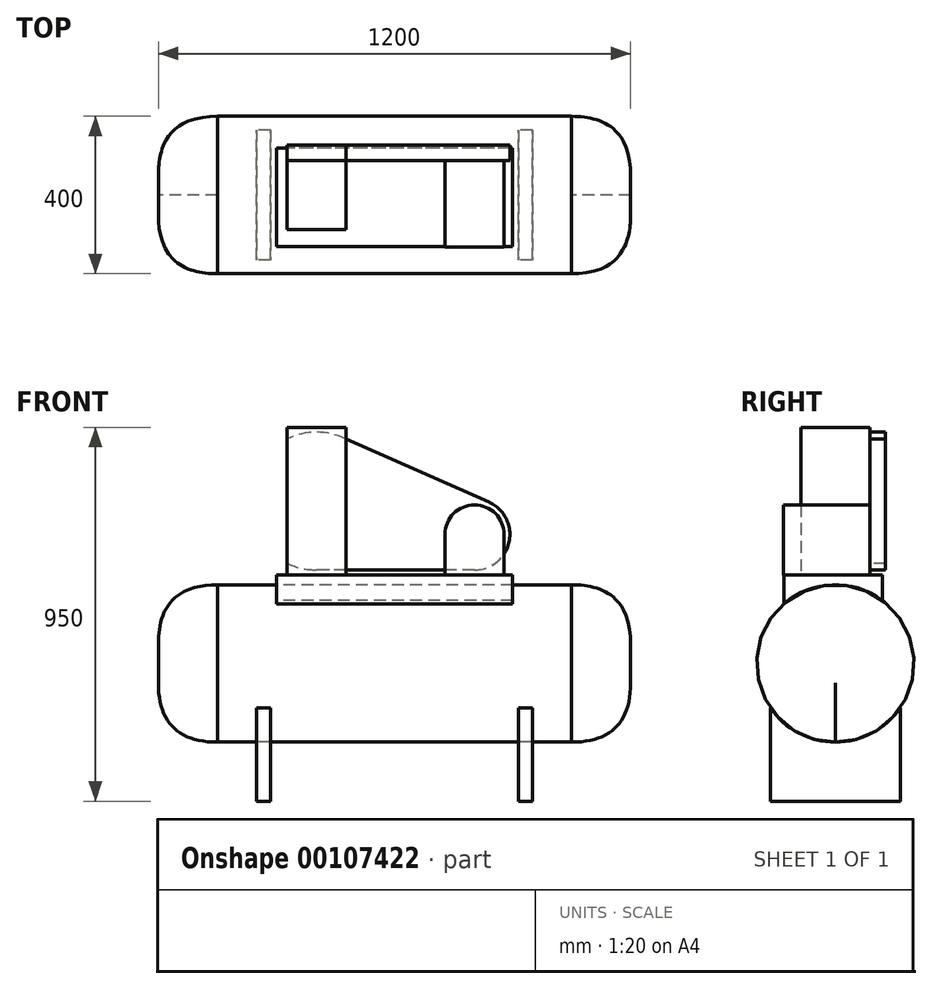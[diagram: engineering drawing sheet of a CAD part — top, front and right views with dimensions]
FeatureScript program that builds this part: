
annotation { "Feature Type Name" : "Feature", "Feature Type Description" : "" }
export const myFeature = defineFeature(function(context is Context, id is Id, definition is map)
    precondition{}
    {
        {
            var Q0;
            Q0=qCreatedBy(makeId("Right.planeOp"),FACE);
            var sketch = newSketch(context, id + "F0", { "sketchPlane" : qUnion([Q0])});
            skCircle(sketch, "E0", {"center": v(0, 0) * mm, "radius": 200 * mm});
            skLineSegment(sketch, "E1", {"start": v(0, 0) * mm, "end": v(0, 200) * mm});
            skLineSegment(sketch, "E2", {"start": v(0, 0) * mm, "end": v(0, -200) * mm});
            skSolve(sketch);
        }
        {
            var Q0;
            Q0=makeQuery(id+"F0.imprint","IMPRINT",FACE,{"disambiguationData":[TD([[makeQuery(id+"F0.imprint","IMPRINT",EDGE,{"derivedFrom":sQuery(id+"F0.wireOp",EDGE,"E0")}),1.0]])]});
            extrude(context, id + "F1", {"entities" : qUnion([Q0]), "endBound" : BoundingType.SYMMETRIC, "depth" : 1200 * mm});
        }
        {
            var Q0;
            Q0=makeQuery(id+"F1.opExtrude","CAP_EDGE",EDGE,{"disambiguationData":[OSD([sQuery(id+"F0.wireOp",EDGE,"E0")])],"isStart":false});
            var Q1;
            Q1=makeQuery(id+"F1.opExtrude","CAP_EDGE",EDGE,{"disambiguationData":[OSD([sQuery(id+"F0.wireOp",EDGE,"E0")])],"isStart":true});
            fillet(context, id + "F2", {"entities" : qUnion([Q0, Q1]), "radius" : 150 * mm, "tangentPropagation" : true, "rho" : .5, "crossSection" : FilletCrossSection.CONIC, "allowEdgeOverflow" : false});
        }
        {
            var Q0;
            Q0=sQuery(id+"F0.wireOp",VERTEX,"E1.end");
            var Q1;
            Q1=sQuery(id+"F0.wireOp",EDGE,"E1");
            cPlane(context, id + "F3", {"entities" : qUnion([Q0, Q1]), "cplaneType" : CPlaneType.LINE_POINT, "offset" : 25 * mm, "width" : 150 * mm, "height" : 150 * mm});
        }
        {
            var Q0;
            Q0=qCreatedBy(id+"F3.planeOp",FACE);
            cPlane(context, id + "F4", {"entities" : qUnion([Q0]), "cplaneType" : CPlaneType.OFFSET, "offset" : 25 * mm, "width" : 150 * mm, "height" : 150 * mm});
        }
        {
            var Q0;
            Q0=qCreatedBy(id+"F4.planeOp",FACE);
            var sketch = newSketch(context, id + "F5", { "sketchPlane" : qUnion([Q0])});
            skLineSegment(sketch, "E3.bottom", {"start": v(300, -130.85) * mm, "end": v(-300, -130.85) * mm});
            skLineSegment(sketch, "E3.top", {"start": v(300, 119.15) * mm, "end": v(-300, 119.15) * mm});
            skLineSegment(sketch, "E3.left", {"start": v(300, -130.85) * mm, "end": v(300, 119.15) * mm});
            skLineSegment(sketch, "E3.right", {"start": v(-300, -130.85) * mm, "end": v(-300, 119.15) * mm});
            skPoint(sketch, "E3.middle", {"position": v(0, -5.85) * mm});
            skSolve(sketch);
        }
        {
            var Q0;
            Q0=makeQuery(id+"F5.imprint","IMPRINT",FACE,{"disambiguationData":[TD([[makeQuery(id+"F5.imprint","IMPRINT",EDGE,{"derivedFrom":sQuery(id+"F5.wireOp",EDGE,"E3.bottom")}),-1.0]])]});
            extrude(context, id + "F6", {"entities" : qUnion([Q0]), "endBound" : BoundingType.UP_TO_NEXT, "oppositeDirection" : true, "depth" : 25 * mm});
        }
        {
            var Q0;
            Q0=makeQuery(id+"F6.opExtrude","CAP_FACE",FACE,{"disambiguationData":[OSD([sQuery(id+"F5.wireOp",EDGE,"E3.bottom"),sQuery(id+"F5.wireOp",EDGE,"E3.top"),sQuery(id+"F5.wireOp",EDGE,"E3.left"),sQuery(id+"F5.wireOp",EDGE,"E3.right")])],"isStart":true});
            var sketch = newSketch(context, id + "F7", { "sketchPlane" : qUnion([Q0])});
            skLineSegment(sketch, "E4.bottom", {"start": v(-273, 87.5) * mm, "end": v(-123, 87.5) * mm});
            skLineSegment(sketch, "E4.top", {"start": v(-273, -87.5) * mm, "end": v(-123, -87.5) * mm});
            skLineSegment(sketch, "E4.left", {"start": v(-273, 87.5) * mm, "end": v(-273, -87.5) * mm});
            skLineSegment(sketch, "E4.right", {"start": v(-123, 87.5) * mm, "end": v(-123, -87.5) * mm});
            skPoint(sketch, "E4.middle", {"position": v(-198, 0) * mm});
            skSolve(sketch);
        }
        {
            var Q0;
            Q0=makeQuery(id+"F7.imprint","IMPRINT",FACE,{"disambiguationData":[TD([[makeQuery(id+"F7.imprint","IMPRINT",EDGE,{"derivedFrom":sQuery(id+"F7.wireOp",EDGE,"E4.bottom")}),-1.0]])]});
            extrude(context, id + "F8", {"entities" : qUnion([Q0]), "depth" : 375 * mm});
        }
        {
            var Q0;
            Q0=makeQuery(id+"F8.opExtrude","SWEPT_FACE",FACE,{"disambiguationData":[OSD([sQuery(id+"F7.wireOp",EDGE,"E4.bottom")])]});
            var sketch = newSketch(context, id + "F9", { "sketchPlane" : qUnion([Q0])});
            skCircle(sketch, "E5", {"center": v(198, 412.5) * mm, "radius": 175 * mm});
            skPoint(sketch, "E5.centerSnap0", {"position": v(198, 600) * mm});
            skPoint(sketch, "E5.centerSnap1", {"position": v(273, 412.5) * mm});
            skCircle(sketch, "E6", {"center": v(-203.22, 327.5) * mm, "radius": 90 * mm});
            skLineSegment(sketch, "E7", {"start": v(-239.72, 409.77) * mm, "end": v(127.04, 572.47) * mm});
            skLineSegment(sketch, "E8", {"start": v(-203.22, 237.5) * mm, "end": v(198, 237.5) * mm});
            skCircle(sketch, "E9", {"center": v(-203.22, 327.5) * mm, "radius": 75 * mm});
            skLineSegment(sketch, "E10.0.0", {"start": v(300, 225) * mm, "end": v(-300, 225) * mm});
            skLineSegment(sketch, "E10.0.2", {"start": v(-300, 225) * mm, "end": v(300, 225) * mm});
            skLineSegment(sketch, "E11", {"start": v(-128.22, 327.5) * mm, "end": v(-128.22, 225) * mm});
            skLineSegment(sketch, "E12", {"start": v(-278.22, 327.5) * mm, "end": v(-278.22, 225) * mm});
            skSolve(sketch);
        }
        {
            var Q0;
            {var subQ0=sQuery(id+"F9.wireOp",EDGE,"E6");var subQ1=makeQuery(id+"F9.imprint","INTERSECT",VERTEX,{"derivedFrom":[subQ0,sQuery(id+"F9.wireOp",EDGE,"E7")]});Q0=makeQuery(id+"F9.imprint","IMPRINT",FACE,{"disambiguationData":[TD([[makeQuery(id+"F9.imprint","IMPRINT",EDGE,{"disambiguationData":[TD([[subQ1,-1.0]])],"derivedFrom":subQ0}),1.0]])]});}
            var Q1;
            {var subQ1=sQuery(id+"F9.wireOp",EDGE,"E6");var subQ7=sQuery(id+"F9.wireOp",EDGE,"E7");var subQ8=makeQuery(id+"F9.imprint","INTERSECT",VERTEX,{"derivedFrom":[subQ1,subQ7]});Q1=makeQuery(id+"F9.imprint","IMPRINT",FACE,{"disambiguationData":[TD([[makeQuery(id+"F9.imprint","IMPRINT",EDGE,{"disambiguationData":[TD([[subQ8,1.0]])],"derivedFrom":subQ1}),-1.0]])]});}
            var Q2;
            {var subQ0=sQuery(id+"F9.wireOp",EDGE,"E5");var subQ1=makeQuery(id+"F8.opExtrude","SWEPT_EDGE",EDGE,{"disambiguationData":[OSD([sQuery(id+"F7.wireOp",EDGE,"E4.bottom"),sQuery(id+"F7.wireOp",EDGE,"E4.right")])]});var subQ2=makeQuery(id+"F9.imprint","INTERSECT",VERTEX,{"disambiguationData":[OD(0.0)],"derivedFrom":[subQ1,subQ0]});Q2=makeQuery(id+"F9.imprint","IMPRINT",FACE,{"disambiguationData":[TD([[makeQuery(id+"F9.imprint","IMPRINT",EDGE,{"disambiguationData":[TD([[subQ2,-1.0]])],"derivedFrom":subQ0}),1.0]])]});}
            var Q3;
            {var subQ0=sQuery(id+"F9.wireOp",EDGE,"E5");var subQ8=makeQuery(id+"F9.imprint","INTERSECT",VERTEX,{"derivedFrom":[subQ0,sQuery(id+"F9.wireOp",EDGE,"E7")]});Q3=makeQuery(id+"F9.imprint","IMPRINT",FACE,{"disambiguationData":[TD([[makeQuery(id+"F9.imprint","IMPRINT",EDGE,{"disambiguationData":[TD([[subQ8,1.0]])],"derivedFrom":subQ0}),1.0]])]});}
            var Q4;
            {var subQ0=sQuery(id+"F9.wireOp",EDGE,"E8");var subQ1=sQuery(id+"F9.wireOp",EDGE,"E5");var subQ2=makeQuery(id+"F9.imprint","INTERSECT",VERTEX,{"derivedFrom":[subQ1,subQ0]});Q4=makeQuery(id+"F9.imprint","IMPRINT",FACE,{"disambiguationData":[TD([[makeQuery(id+"F9.imprint","IMPRINT",EDGE,{"disambiguationData":[TD([[subQ2,1.0]])],"derivedFrom":subQ1}),-1.0]])]});}
            var Q5;
            {var subQ0=sQuery(id+"F9.wireOp",EDGE,"E5");var subQ1=makeQuery(id+"F8.opExtrude","SWEPT_EDGE",EDGE,{"disambiguationData":[OSD([sQuery(id+"F7.wireOp",EDGE,"E4.bottom"),sQuery(id+"F7.wireOp",EDGE,"E4.left")])]});var subQ2=makeQuery(id+"F9.imprint","INTERSECT",VERTEX,{"disambiguationData":[OD(0.0)],"derivedFrom":[subQ1,subQ0]});Q5=makeQuery(id+"F9.imprint","IMPRINT",FACE,{"disambiguationData":[TD([[makeQuery(id+"F9.imprint","IMPRINT",EDGE,{"disambiguationData":[TD([[subQ2,1.0]])],"derivedFrom":subQ0}),1.0]])]});}
            var Q6;
            Q6=makeQuery(id+"F9.imprint","IMPRINT",FACE,{"disambiguationData":[TD([[makeQuery(id+"F9.imprint","IMPRINT",EDGE,{"derivedFrom":sQuery(id+"F9.wireOp",EDGE,"E9")}),1.0]])]});
            var Q7;
            {var subQ5=sQuery(id+"F9.wireOp",EDGE,"E6");var subQ7=makeQuery(id+"F9.imprint","INTERSECT",VERTEX,{"derivedFrom":[subQ5,sQuery(id+"F9.wireOp",EDGE,"E8")]});Q7=makeQuery(id+"F9.imprint","IMPRINT",FACE,{"disambiguationData":[TD([[makeQuery(id+"F9.imprint","IMPRINT",EDGE,{"disambiguationData":[TD([[subQ7,1.0]])],"derivedFrom":subQ5}),1.0]])]});}
            var Q8;
            {var subQ0=sQuery(id+"F9.wireOp",EDGE,"E8");var subQ1=sQuery(id+"F9.wireOp",EDGE,"E6");var subQ2=makeQuery(id+"F9.imprint","INTERSECT",VERTEX,{"derivedFrom":[subQ1,subQ0]});Q8=makeQuery(id+"F9.imprint","IMPRINT",FACE,{"disambiguationData":[TD([[makeQuery(id+"F9.imprint","IMPRINT",EDGE,{"disambiguationData":[TD([[subQ2,-1.0]])],"derivedFrom":subQ1}),-1.0]])]});}
            extrude(context, id + "F10", {"entities" : qUnion([Q0, Q1, Q2, Q3, Q4, Q5, Q6, Q7, Q8]), "depth" : 40 * mm});
        }
        {
            var Q0;
            Q0=makeQuery(id+"F9.imprint","IMPRINT",FACE,{"disambiguationData":[TD([[makeQuery(id+"F9.imprint","IMPRINT",EDGE,{"derivedFrom":sQuery(id+"F9.wireOp",EDGE,"E9")}),1.0]])]});
            var Q1;
            {var subQ0=sQuery(id+"F9.wireOp",EDGE,"E8");var subQ1=sQuery(id+"F9.wireOp",EDGE,"E6");var subQ2=makeQuery(id+"F9.imprint","INTERSECT",VERTEX,{"derivedFrom":[subQ1,subQ0]});Q1=makeQuery(id+"F9.imprint","IMPRINT",FACE,{"disambiguationData":[TD([[makeQuery(id+"F9.imprint","IMPRINT",EDGE,{"disambiguationData":[TD([[subQ2,-1.0]])],"derivedFrom":subQ1}),-1.0]])]});}
            var Q2;
            {var subQ5=sQuery(id+"F9.wireOp",EDGE,"E6");var subQ7=makeQuery(id+"F9.imprint","INTERSECT",VERTEX,{"derivedFrom":[subQ5,sQuery(id+"F9.wireOp",EDGE,"E8")]});Q2=makeQuery(id+"F9.imprint","IMPRINT",FACE,{"disambiguationData":[TD([[makeQuery(id+"F9.imprint","IMPRINT",EDGE,{"disambiguationData":[TD([[subQ7,1.0]])],"derivedFrom":subQ5}),1.0]])]});}
            var Q3;
            {var subQ5=sQuery(id+"F9.wireOp",EDGE,"E8");var subQ6=sQuery(id+"F9.wireOp",EDGE,"E6");var subQ7=makeQuery(id+"F9.imprint","INTERSECT",VERTEX,{"derivedFrom":[subQ6,subQ5]});Q3=makeQuery(id+"F9.imprint","IMPRINT",FACE,{"disambiguationData":[TD([[makeQuery(id+"F9.imprint","IMPRINT",EDGE,{"disambiguationData":[TD([[subQ7,1.0]])],"derivedFrom":subQ6}),-1.0]])]});}
            extrude(context, id + "F11", {"entities" : qUnion([Q0, Q1, Q2, Q3]), "oppositeDirection" : true, "depth" : 220 * mm});
        }
        {
            var Q0;
            Q0=sQuery(id+"F0.wireOp",VERTEX,"E2.end");
            var Q1;
            Q1=sQuery(id+"F0.wireOp",EDGE,"E2");
            cPlane(context, id + "F12", {"entities" : qUnion([Q0, Q1]), "cplaneType" : CPlaneType.LINE_POINT, "offset" : 25 * mm, "width" : 150 * mm, "height" : 150 * mm});
        }
        {
            var Q0;
            Q0=qCreatedBy(id+"F12.planeOp",FACE);
            cPlane(context, id + "F13", {"entities" : qUnion([Q0]), "cplaneType" : CPlaneType.OFFSET, "offset" : 150 * mm, "width" : 150 * mm, "height" : 150 * mm});
        }
        {
            var Q0;
            Q0=qCreatedBy(id+"F13.planeOp",FACE);
            var sketch = newSketch(context, id + "F14", { "sketchPlane" : qUnion([Q0])});
            skLineSegment(sketch, "E13.bottom", {"start": v(315.41, -165.12) * mm, "end": v(350, -165.12) * mm});
            skLineSegment(sketch, "E13.top", {"start": v(315.41, 165.12) * mm, "end": v(350, 165.12) * mm});
            skLineSegment(sketch, "E13.left", {"start": v(315.41, -165.12) * mm, "end": v(315.41, 165.12) * mm});
            skLineSegment(sketch, "E13.right", {"start": v(350, -165.12) * mm, "end": v(350, 165.12) * mm});
            skPoint(sketch, "E13.middle", {"position": v(332.7, 0) * mm});
            skLineSegment(sketch, "E14.0", {"start": v(0, 200) * mm, "end": v(0, -200) * mm});
            skLineSegment(sketch, "E15.MirrorCS", {"start": v(-315.41, -165.12) * mm, "end": v(-315.41, 165.12) * mm});
            skLineSegment(sketch, "E16.MirrorCS", {"start": v(-315.41, 165.12) * mm, "end": v(-350, 165.12) * mm});
            skLineSegment(sketch, "E17.MirrorCS", {"start": v(-350, -165.12) * mm, "end": v(-350, 165.12) * mm});
            skLineSegment(sketch, "E18.MirrorCS", {"start": v(-315.41, -165.12) * mm, "end": v(-350, -165.12) * mm});
            skSolve(sketch);
        }
        {
            var Q0;
            Q0=makeQuery(id+"F14.imprint","IMPRINT",FACE,{"disambiguationData":[TD([[makeQuery(id+"F14.imprint","IMPRINT",EDGE,{"derivedFrom":sQuery(id+"F14.wireOp",EDGE,"E13.bottom")}),1.0]])]});
            var Q1;
            Q1=makeQuery(id+"F14.imprint","IMPRINT",FACE,{"disambiguationData":[TD([[makeQuery(id+"F14.imprint","IMPRINT",EDGE,{"derivedFrom":sQuery(id+"F14.wireOp",EDGE,"E15.MirrorCS")}),1.0]])]});
            extrude(context, id + "F15", {"entities" : qUnion([Q0, Q1]), "endBound" : BoundingType.UP_TO_NEXT, "oppositeDirection" : true, "depth" : 25 * mm});
        }
    });
